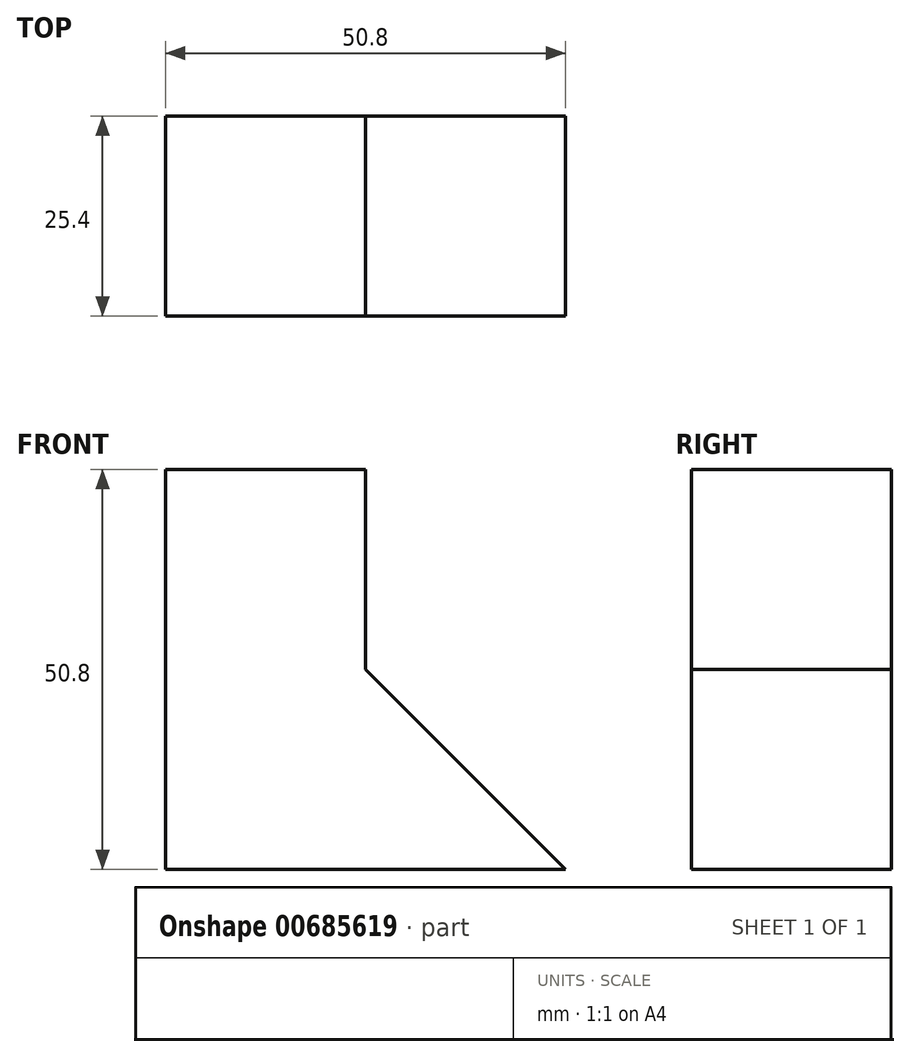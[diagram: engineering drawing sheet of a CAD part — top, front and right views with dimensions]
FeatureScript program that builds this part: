
annotation { "Feature Type Name" : "Feature", "Feature Type Description" : "" }
export const myFeature = defineFeature(function(context is Context, id is Id, definition is map)
    precondition{}
    {
        {
            var Q0;
            Q0=qCreatedBy(makeId("Front.planeOp"),FACE);
            var sketch = newSketch(context, id + "F0", { "sketchPlane" : qUnion([Q0])});
            skLineSegment(sketch, "E0", {"start": v(-61.72, 50.8) * mm, "end": v(-61.72, 0) * mm});
            skLineSegment(sketch, "E1", {"start": v(-61.72, 0) * mm, "end": v(-10.92, 0) * mm});
            skLineSegment(sketch, "E2", {"start": v(-61.72, 50.8) * mm, "end": v(-36.32, 50.8) * mm});
            skLineSegment(sketch, "E3", {"start": v(-36.32, 50.8) * mm, "end": v(-36.32, 25.4) * mm});
            skLineSegment(sketch, "E4", {"start": v(-36.32, 25.4) * mm, "end": v(-10.92, 0) * mm});
            skSolve(sketch);
        }
        {
            var Q0;
            Q0 = qSketchRegion(id + "F0", true);
            extrude(context, id + "F1", {"entities" : qUnion([Q0]), "depth" : 25.4 * mm, "offsetDistance" : 25.4 * mm});
        }
    });
